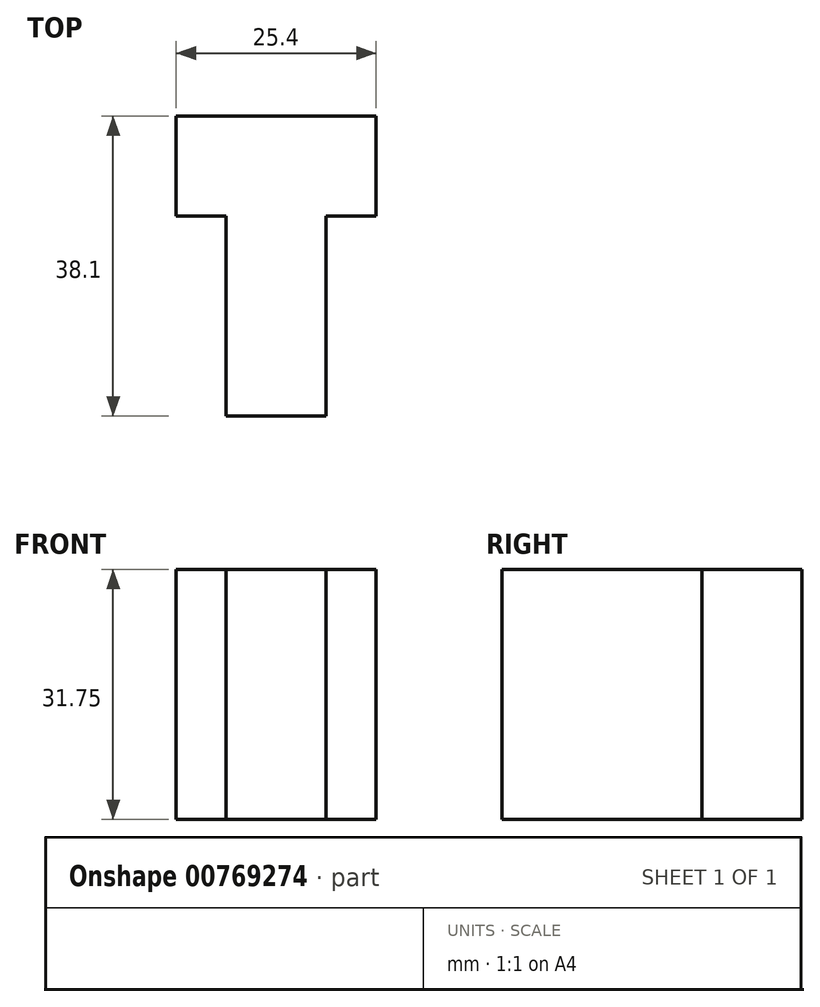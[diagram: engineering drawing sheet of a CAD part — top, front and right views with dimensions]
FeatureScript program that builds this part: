
annotation { "Feature Type Name" : "Feature", "Feature Type Description" : "" }
export const myFeature = defineFeature(function(context is Context, id is Id, definition is map)
    precondition{}
    {
        {
            var Q0;
            Q0=qCreatedBy(makeId("Top.planeOp"),FACE);
            var sketch = newSketch(context, id + "F0", { "sketchPlane" : qUnion([Q0])});
            skLineSegment(sketch, "E0", {"start": v(0, 0) * mm, "end": v(12.7, 0) * mm});
            skLineSegment(sketch, "E1", {"start": v(12.7, 0) * mm, "end": v(12.7, 25.4) * mm});
            skLineSegment(sketch, "E2", {"start": v(12.7, 25.4) * mm, "end": v(19.05, 25.4) * mm});
            skLineSegment(sketch, "E3", {"start": v(19.05, 25.4) * mm, "end": v(19.05, 38.1) * mm});
            skLineSegment(sketch, "E4", {"start": v(19.05, 38.1) * mm, "end": v(-6.35, 38.1) * mm});
            skLineSegment(sketch, "E5", {"start": v(-6.35, 38.1) * mm, "end": v(-6.35, 25.4) * mm});
            skLineSegment(sketch, "E6", {"start": v(-6.35, 25.4) * mm, "end": v(0, 25.4) * mm});
            skLineSegment(sketch, "E7", {"start": v(0, 25.4) * mm, "end": v(0, 0) * mm});
            skSolve(sketch);
        }
        {
            var Q0;
            Q0 = qSketchRegion(id + "F0", true);
            extrude(context, id + "F1", {"entities" : qUnion([Q0]), "depth" : 31.75 * mm, "offsetDistance" : 25.4 * mm});
        }
    });
